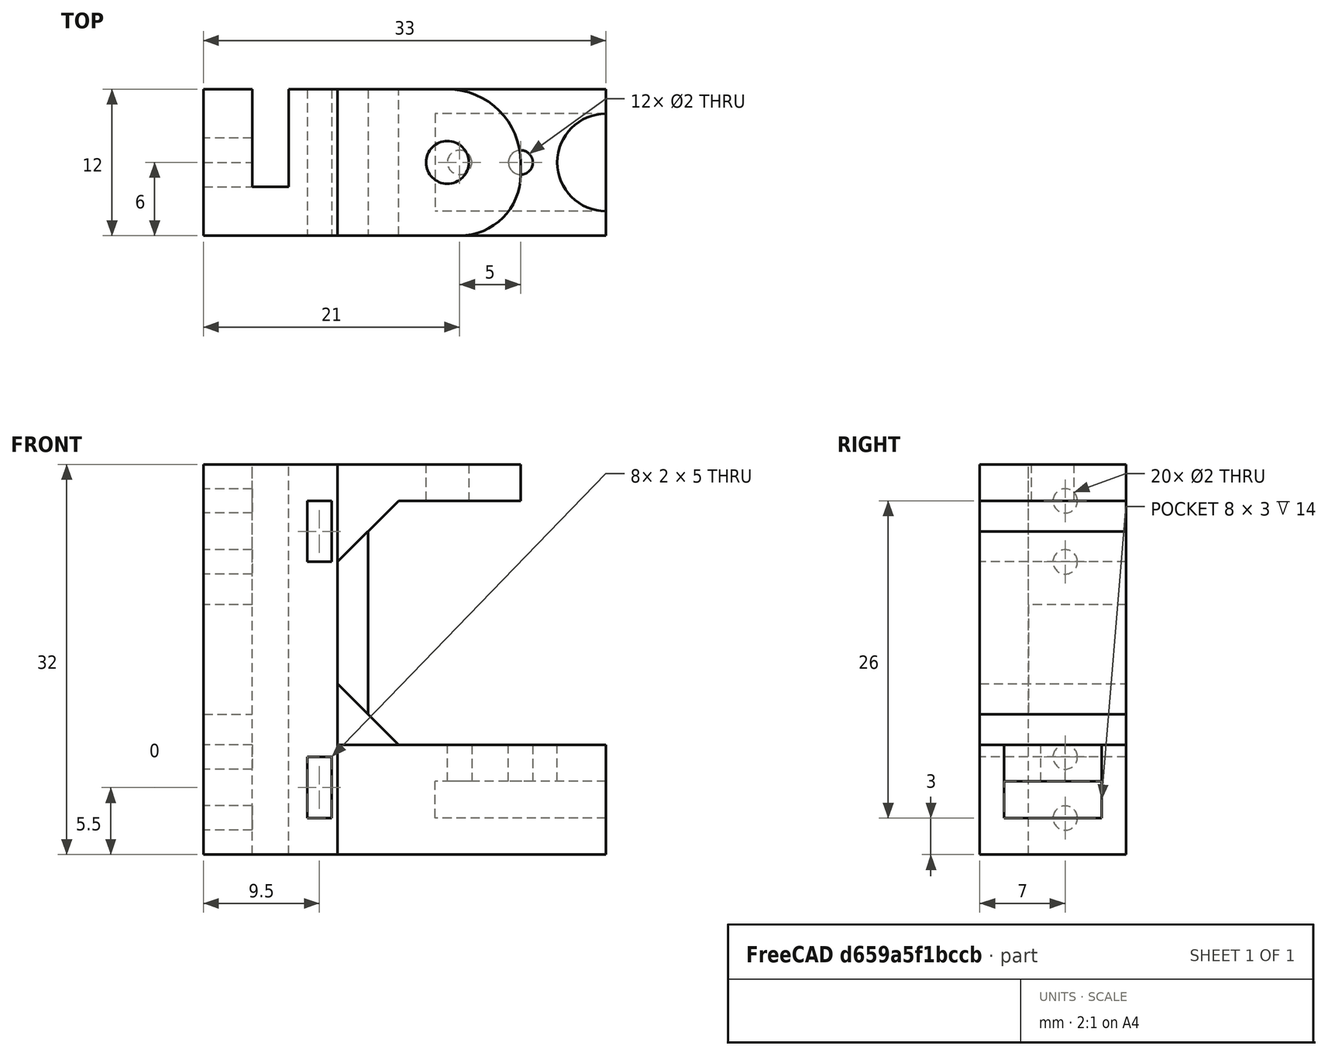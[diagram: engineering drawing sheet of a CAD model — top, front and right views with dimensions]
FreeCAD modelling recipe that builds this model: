
FCSTD DOCUMENT  (FreeCAD 0.17R8884 (Git))
Label: cuello2
License: CC-BY 3.0
LicenseURL: http://creativecommons.org/licenses/by/3.0/
objects: Sketcher::SketchObject×11, PartDesign::Pocket×7, PartDesign::Pad×4, Part::Feature×3, Mesh::Feature×2, PartDesign::Fillet×2, PartDesign::Chamfer×2
note: 40 computed .brp shape members not serialized (recipe doc carries the construction recipe); baked Part::Feature solids carry a one-line shape summary decoded from their .brp

FEATURE [Sketcher::SketchObject] Sketch
  MapMode = 5
  sketch-geometry (8):
    g0: LineSegment StartX=4 StartY=12 StartZ=0 EndX=0 EndY=12 EndZ=0
    g1: LineSegment StartX=0 StartY=12 StartZ=0 EndX=0 EndY=0 EndZ=0
    g2: LineSegment StartX=0 StartY=0 StartZ=0 EndX=11 EndY=0 EndZ=0
    g3: LineSegment StartX=11 StartY=0 StartZ=0 EndX=11 EndY=12 EndZ=0
    g4: LineSegment StartX=11 StartY=12 StartZ=0 EndX=7 EndY=12 EndZ=0
    g5: LineSegment StartX=7 StartY=12 StartZ=0 EndX=7 EndY=4 EndZ=0
    g6: LineSegment StartX=7 StartY=4 StartZ=0 EndX=4 EndY=4 EndZ=0
    g7: LineSegment StartX=4 StartY=4 StartZ=0 EndX=4 EndY=12 EndZ=0
  constraints (23):
    c: Horizontal(g0)
    c: Coincident(g0,g1)
    c: Vertical(g1)
    c: Coincident(g1,g2)
    c: Horizontal(g2)
    c: Coincident(g2,g3)
    c: Vertical(g3)
    c: Coincident(g3,g4)
    c: Horizontal(g4)
    c: Coincident(g4,g5)
    c: Vertical(g5)
    c: Coincident(g5,g6)
    c: Horizontal(g6)
    c: Coincident(g6,g7)
    c: Vertical(g7)
    c: Coincident(g7,g0)
    c: Equal(g0,g4)
    c: DistanceX(g0) = -4
    c: Distance(g6,g2) = 4
    c: DistanceX(g6) = -3
    c: Equal(g7,g5)
    c: DistanceY(g5) = -8
    c: Coincident(g1,g-1)
FEATURE [PartDesign::Pad] Pad
  Length = 32
  Length2 = 100
  Profile = -> Sketch
  Type = 0
FEATURE [Sketcher::SketchObject] Sketch001
  ExternalGeometry = -> [Pad]
  MapMode = 5
  Placement = pos=(0,12,0) rot=(0,0.707107,0.707107;3.14159rad)
  Support = -> [Pad]
  sketch-geometry (6):
    g0: LineSegment StartX=-4 StartY=20.5 StartZ=0 EndX=0 EndY=20.5 EndZ=0
    g1: LineSegment StartX=0 StartY=20.5 StartZ=0 EndX=0 EndY=11.5 EndZ=0
    g2: LineSegment StartX=0 StartY=11.5 StartZ=0 EndX=-4 EndY=11.5 EndZ=0
    g3: LineSegment StartX=-4 StartY=11.5 StartZ=0 EndX=-4 EndY=20.5 EndZ=0
    g4: LineSegment [constr] StartX=-4 StartY=32 StartZ=0 EndX=-4 EndY=20.5 EndZ=0
    g5: LineSegment [constr] StartX=-4 StartY=11.5 StartZ=0 EndX=-4 EndY=0 EndZ=0
  constraints (17):
    c: Coincident(g0,g1)
    c: Coincident(g1,g2)
    c: Coincident(g2,g3)
    c: Coincident(g3,g0)
    c: Horizontal(g0)
    c: Horizontal(g2)
    c: Vertical(g1)
    c: Vertical(g3)
    c: DistanceY(g3) = 9
    c: Vertical(g4)
    c: Vertical(g5)
    c: Equal(g4,g5)
    c: Coincident(g5,g-3)
    c: Coincident(g5,g2)
    c: Coincident(g4,g0)
    c: Coincident(g4,g-3)
    c: PointOnObject(g1,g-2)
FEATURE [PartDesign::Pocket] Pocket
  Length = 8
  Profile = -> Sketch001
  Type = 0
FEATURE [Sketcher::SketchObject] Sketch002
  ExternalGeometry = -> [Pocket]
  MapMode = 5
  Placement = pos=(11,0,0) rot=(0.57735,0.57735,0.57735;2.0944rad)
  Support = -> [Pocket]
  sketch-geometry (4):
    g0: LineSegment StartX=0 StartY=9 StartZ=0 EndX=12 EndY=9 EndZ=0
    g1: LineSegment StartX=12 StartY=9 StartZ=0 EndX=12 EndY=0 EndZ=0
    g2: LineSegment StartX=12 StartY=0 StartZ=0 EndX=0 EndY=0 EndZ=0
    g3: LineSegment StartX=0 StartY=0 StartZ=0 EndX=0 EndY=9 EndZ=0
  constraints (11):
    c: Coincident(g0,g1)
    c: Coincident(g1,g2)
    c: Coincident(g2,g3)
    c: Coincident(g3,g0)
    c: Horizontal(g0)
    c: Horizontal(g2)
    c: Vertical(g1)
    c: Vertical(g3)
    c: Coincident(g1,g-3)
    c: Coincident(g2,g-1)
    c: DistanceY(g3) = 9
FEATURE [PartDesign::Pad] Pad001
  Length = 22
  Length2 = 100
  Profile = -> Sketch002
  Type = 0
FEATURE [Part::Feature] Pad001001  label="Pad002"
  shape: bbox 33 x 12 x 32 mm, 16 faces (baked)
FEATURE [Sketcher::SketchObject] Sketch003
  ExternalGeometry = -> [Pad001001]
  MapMode = 5
  Placement = pos=(33,0,0) rot=(0.57735,0.57735,0.57735;2.0944rad)
  Support = -> [Pad001001]
  sketch-geometry (4):
    g0: LineSegment StartX=2 StartY=6 StartZ=0 EndX=10 EndY=6 EndZ=0
    g1: LineSegment StartX=10 StartY=6 StartZ=0 EndX=10 EndY=3 EndZ=0
    g2: LineSegment StartX=10 StartY=3 StartZ=0 EndX=2 EndY=3 EndZ=0
    g3: LineSegment StartX=2 StartY=3 StartZ=0 EndX=2 EndY=6 EndZ=0
  constraints (12):
    c: Coincident(g0,g1)
    c: Coincident(g1,g2)
    c: Coincident(g2,g3)
    c: Coincident(g3,g0)
    c: Horizontal(g0)
    c: Horizontal(g2)
    c: Vertical(g1)
    c: Vertical(g3)
    c: DistanceX(g2) = -8
    c: DistanceY(g3) = 3
    c: Distance(g0,g-3) = 3
    c: Distance(g1,g-4) = 2
FEATURE [PartDesign::Pocket] Pocket001
  Length = 14
  Profile = -> Sketch003
  Type = 0
FEATURE [Mesh::Feature] _g_servo  label="9g_servo"
  Placement = pos=(-15,6,21) rot=(0,1,0;1.5708rad)
FEATURE [Mesh::Feature] _g_servo001  label="9g_servo001"
  Placement = pos=(37,6,26) rot=(0,1,0;3.14159rad)
FEATURE [Sketcher::SketchObject] Sketch004
  ExternalGeometry = -> [Pocket001]
  MapMode = 5
  Placement = pos=(0,0,9) rot=(0,0,1;0rad)
  Support = -> [Pocket001]
  sketch-geometry (4):
    g0: ArcOfCircle CenterX=33 CenterY=6 CenterZ=0 NormalX=0 NormalY=0 NormalZ=1 Radius=4 StartAngle=1.5708 EndAngle=4.71239
    g1: LineSegment [constr] StartX=33 StartY=12 StartZ=0 EndX=33 EndY=10 EndZ=0
    g2: LineSegment [constr] StartX=33 StartY=2 StartZ=0 EndX=33 EndY=0 EndZ=0
    g3: LineSegment StartX=33 StartY=10 StartZ=0 EndX=33 EndY=2 EndZ=0
  constraints (12):
    c: PointOnObject(g0,g-3)
    c: Radius(g0) = 4
    c: Vertical(g1)
    c: Vertical(g2)
    c: Equal(g1,g2)
    c: Coincident(g2,g0)
    c: Coincident(g2,g-3)
    c: Coincident(g1,g0)
    c: Coincident(g1,g-3)
    c: Vertical(g3)
    c: Coincident(g3,g0)
    c: Coincident(g3,g0)
FEATURE [PartDesign::Pocket] Pocket002
  Length = 5
  Profile = -> Sketch004
  Type = 0
FEATURE [Sketcher::SketchObject] Sketch005
  ExternalGeometry = -> [Pocket002]
  MapMode = 5
  Placement = pos=(11,0,0) rot=(0.57735,0.57735,0.57735;2.0944rad)
  Support = -> [Pocket002]
  sketch-geometry (4):
    g0: LineSegment StartX=0 StartY=32 StartZ=0 EndX=12 EndY=32 EndZ=0
    g1: LineSegment StartX=12 StartY=32 StartZ=0 EndX=12 EndY=29 EndZ=0
    g2: LineSegment StartX=12 StartY=29 StartZ=0 EndX=0 EndY=29 EndZ=0
    g3: LineSegment StartX=0 StartY=29 StartZ=0 EndX=0 EndY=32 EndZ=0
  constraints (11):
    c: Coincident(g0,g1)
    c: Coincident(g1,g2)
    c: Coincident(g2,g3)
    c: Coincident(g3,g0)
    c: Horizontal(g0)
    c: Horizontal(g2)
    c: Vertical(g1)
    c: Vertical(g3)
    c: DistanceY(g1) = -3
    c: Coincident(g0,g-3)
    c: Coincident(g0,g-3)
FEATURE [PartDesign::Pad] Pad001002
  Length = 15
  Length2 = 100
  Profile = -> Sketch005
  Type = 0
FEATURE [PartDesign::Fillet] Fillet
  Base = -> Pad001002 [Edge53]
  Radius = 6
FEATURE [PartDesign::Fillet] Fillet001
  Base = -> Fillet [Edge20]
  Radius = 5
FEATURE [PartDesign::Chamfer] Chamfer
  Base = -> Fillet001 [Edge52]
  Size = 5
FEATURE [PartDesign::Chamfer] Chamfer001
  Base = -> Chamfer [Edge26]
  Size = 5
FEATURE [Sketcher::SketchObject] Sketch006
  ExternalGeometry = -> [Chamfer001]
  MapMode = 5
  Placement = pos=(0,0,9) rot=(0,0,1;0rad)
  Support = -> [Chamfer001]
  sketch-geometry (3):
    g0: Circle CenterX=21 CenterY=6 CenterZ=0 NormalX=0 NormalY=0 NormalZ=1 Radius=1
    g1: Circle CenterX=26 CenterY=6 CenterZ=0 NormalX=0 NormalY=0 NormalZ=1 Radius=1
    g2: LineSegment [constr] StartX=16 StartY=6 StartZ=0 EndX=33 EndY=6 EndZ=0
  constraints (9):
    c: Horizontal(g2)
    c: Coincident(g2,g-3)
    c: PointOnObject(g2,g-4)
    c: PointOnObject(g1,g2)
    c: PointOnObject(g0,g2)
    c: Radius(g1) = 1
    c: Radius(g0) = 1
    c: Distance(g0,g1) = 5
    c: Distance(g0,g2) = 5
FEATURE [PartDesign::Pocket] Pocket003
  Length = 5
  Profile = -> Sketch006
  Type = 0
FEATURE [Sketcher::SketchObject] Sketch007
  ExternalGeometry = -> [Pocket003]
  MapMode = 5
  Placement = pos=(0,0,0) rot=(0.57735,-0.57735,-0.57735;2.0944rad)
  Support = -> [Pocket003]
  sketch-geometry (5):
    g0: Circle CenterX=-7 CenterY=29 CenterZ=0 NormalX=0 NormalY=0 NormalZ=1 Radius=1
    g1: Circle CenterX=-7 CenterY=24 CenterZ=0 NormalX=0 NormalY=0 NormalZ=1 Radius=1
    g2: Circle CenterX=-7 CenterY=8 CenterZ=0 NormalX=0 NormalY=0 NormalZ=1 Radius=1
    g3: Circle CenterX=-7 CenterY=3 CenterZ=0 NormalX=0 NormalY=0 NormalZ=1 Radius=1
    g4: LineSegment [constr] StartX=-7 StartY=32 StartZ=0 EndX=-7 EndY=0 EndZ=0
  constraints (16):
    c: Vertical(g4)
    c: PointOnObject(g4,g-1)
    c: PointOnObject(g4,g-3)
    c: Radius(g0) = 1
    c: Radius(g1) = 1
    c: Radius(g2) = 1
    c: Radius(g3) = 1
    c: PointOnObject(g0,g4)
    c: PointOnObject(g1,g4)
    c: PointOnObject(g2,g4)
    c: PointOnObject(g3,g4)
    c: Distance(g0,g1) = 5
    c: Distance(g2,g3) = 5
    c: Distance(g0,g4) = 3
    c: Distance(g3,g4) = 3
    c: Distance(g4,g-3) = 5
FEATURE [PartDesign::Pocket] Pocket004
  Length = 5
  Profile = -> Sketch007
  Type = 0
FEATURE [Sketcher::SketchObject] Sketch008
  ExternalGeometry = -> [Pocket004]
  MapMode = 5
  Placement = pos=(0,12,0) rot=(0,0.707107,0.707107;3.14159rad)
  Support = -> [Pocket004]
  sketch-geometry (9):
    g0: LineSegment StartX=-10.5 StartY=29 StartZ=0 EndX=-8.5 EndY=29 EndZ=0
    g1: LineSegment StartX=-8.5 StartY=29 StartZ=0 EndX=-8.5 EndY=24 EndZ=0
    g2: LineSegment StartX=-8.5 StartY=24 StartZ=0 EndX=-10.5 EndY=24 EndZ=0
    g3: LineSegment StartX=-10.5 StartY=24 StartZ=0 EndX=-10.5 EndY=29 EndZ=0
    g4: LineSegment StartX=-10.5 StartY=8 StartZ=0 EndX=-8.5 EndY=8 EndZ=0
    g5: LineSegment StartX=-8.5 StartY=8 StartZ=0 EndX=-8.5 EndY=3 EndZ=0
    g6: LineSegment StartX=-8.5 StartY=3 StartZ=0 EndX=-10.5 EndY=3 EndZ=0
    g7: LineSegment StartX=-10.5 StartY=3 StartZ=0 EndX=-10.5 EndY=8 EndZ=0
    g8: LineSegment [constr] StartX=-8.5 StartY=24 StartZ=0 EndX=-8.5 EndY=8 EndZ=0
  constraints (26):
    c: Coincident(g0,g1)
    c: Coincident(g1,g2)
    c: Coincident(g2,g3)
    c: Coincident(g3,g0)
    c: Horizontal(g0)
    c: Horizontal(g2)
    c: Vertical(g1)
    c: Vertical(g3)
    c: Coincident(g4,g5)
    c: Coincident(g5,g6)
    c: Coincident(g6,g7)
    c: Coincident(g7,g4)
    c: Horizontal(g4)
    c: Horizontal(g6)
    c: Vertical(g5)
    c: Vertical(g7)
    c: Equal(g7,g3)
    c: Equal(g2,g4)
    c: Vertical(g8)
    c: Coincident(g8,g1)
    c: Coincident(g8,g4)
    c: DistanceX(g6) = -2
    c: DistanceY(g7) = 5
    c: DistanceY(g-1,g6) = 3
    c: Distance(g0,g-3) = 3
    c: Distance(g4,g-4) = 1.5
FEATURE [PartDesign::Pocket] Pocket005
  Length = 14
  Profile = -> Sketch008
  Type = 0
FEATURE [Part::Feature] Pocket005001  label="Pocket006"
  shape: bbox 33 x 12 x 32 mm, 42 faces (baked)
FEATURE [Sketcher::SketchObject] Sketch009
  ExternalGeometry = -> [Pocket005001]
  MapMode = 5
  Placement = pos=(0,12,0) rot=(0,0.707107,0.707107;3.14159rad)
  Support = -> [Pocket005001]
  sketch-geometry (4):
    g0: LineSegment StartX=-11 StartY=24 StartZ=0 EndX=-13.5 EndY=26.5 EndZ=0
    g1: LineSegment StartX=-13.5 StartY=26.5 StartZ=0 EndX=-13.5 EndY=11.5 EndZ=0
    g2: LineSegment StartX=-13.5 StartY=11.5 StartZ=0 EndX=-11 EndY=14 EndZ=0
    g3: LineSegment StartX=-11 StartY=14 StartZ=0 EndX=-11 EndY=24 EndZ=0
  constraints (11):
    c: Coincident(g0,g1)
    c: Coincident(g1,g2)
    c: Coincident(g2,g3)
    c: Vertical(g3)
    c: Coincident(g3,g0)
    c: Coincident(g0,g-5)
    c: Coincident(g2,g-5)
    c: PointOnObject(g0,g-3)
    c: PointOnObject(g1,g-4)
    c: DistanceY(g1) = -15
    c: Vertical(g1)
FEATURE [PartDesign::Pad] Pad001003
  Length = 12
  Length2 = 100
  Profile = -> Sketch009
  Reversed = true
  Type = 0
FEATURE [Part::Feature] Pad001003001  label="Pad001004"
  shape: bbox 33 x 12 x 32 mm, 42 faces (baked)
FEATURE [Sketcher::SketchObject] Sketch010
  ExternalGeometry = -> [Pad001003001]
  MapMode = 5
  Placement = pos=(0,0,32) rot=(0,0,1;0rad)
  Support = -> [Pad001003001]
  sketch-geometry (1):
    g0: Circle CenterX=20 CenterY=6 CenterZ=0 NormalX=0 NormalY=0 NormalZ=1 Radius=1.75
  constraints (2):
    c: Coincident(g-3,g0)
    c: Radius(g0) = 1.75
FEATURE [PartDesign::Pocket] Pocket005002
  Length = 4
  Profile = -> Sketch010
  Type = 0
